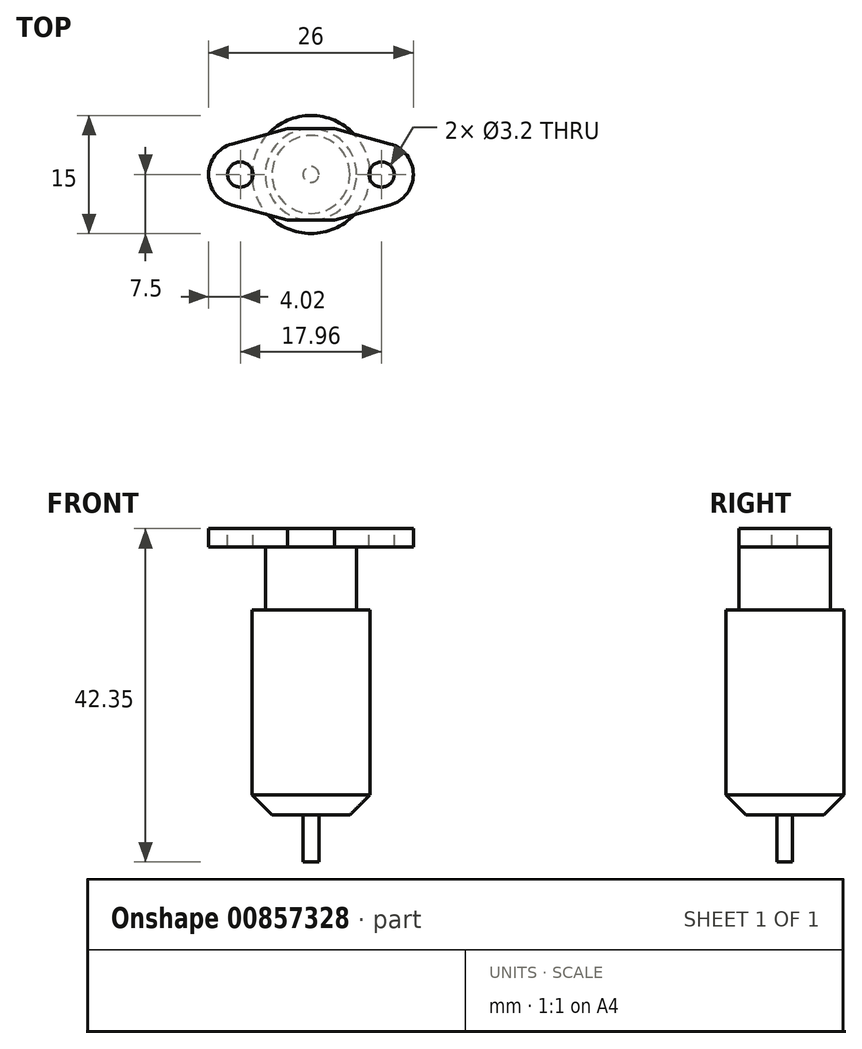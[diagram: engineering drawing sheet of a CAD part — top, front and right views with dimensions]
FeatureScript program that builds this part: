
annotation { "Feature Type Name" : "Feature", "Feature Type Description" : "" }
export const myFeature = defineFeature(function(context is Context, id is Id, definition is map)
    precondition{}
    {
        {
            var Q0;
            Q0=qCreatedBy(makeId("Top.planeOp"),FACE);
            var sketch = newSketch(context, id + "F0", { "sketchPlane" : qUnion([Q0])});
            skCircle(sketch, "E0", {"center": v(-8.98, 0) * mm, "radius": 1.6 * mm});
            skCircle(sketch, "E1", {"center": v(8.98, 0) * mm, "radius": 1.6 * mm});
            skArc(sketch, "E2", {"start": v(10.05, -3.88) * mm, "mid": v(13, 0) * mm, "end": v(10.05, 3.88) * mm});
            skArc(sketch, "E3", {"start": v(-10.05, 3.88) * mm, "mid": v(-13, 0) * mm, "end": v(-10.05, -3.88) * mm});
            skLineSegment(sketch, "E4", {"start": v(-3, 5.82) * mm, "end": v(3, 5.82) * mm});
            skLineSegment(sketch, "E5", {"start": v(-3, -5.82) * mm, "end": v(3, -5.82) * mm});
            skLineSegment(sketch, "E6", {"start": v(-3, 5.82) * mm, "end": v(-10.05, 3.88) * mm});
            skLineSegment(sketch, "E7", {"start": v(3, 5.82) * mm, "end": v(10.05, 3.88) * mm});
            skLineSegment(sketch, "E8", {"start": v(10.05, -3.88) * mm, "end": v(3, -5.82) * mm});
            skLineSegment(sketch, "E9", {"start": v(-3, -5.82) * mm, "end": v(-10.05, -3.88) * mm});
            skSolve(sketch);
        }
        {
            var Q0;
            Q0=makeQuery(id+"F0.imprint","IMPRINT",FACE,{"disambiguationData":[TD([[makeQuery(id+"F0.imprint","IMPRINT",EDGE,{"derivedFrom":sQuery(id+"F0.wireOp",EDGE,"E0")}),-1.0]])]});
            extrude(context, id + "F1", {"entities" : qUnion([Q0]), "oppositeDirection" : true, "depth" : 2.3 * mm, "offsetDistance" : 25 * mm});
        }
        {
            var Q0;
            Q0=qCreatedBy(makeId("Front.planeOp"),FACE);
            var sketch = newSketch(context, id + "F2", { "sketchPlane" : qUnion([Q0])});
            skPoint(sketch, "E10.0", {"position": v(0, -2.3) * mm});
            skLineSegment(sketch, "E11", {"start": v(0, -2.3) * mm, "end": v(5.8, -2.3) * mm});
            skLineSegment(sketch, "E12", {"start": v(5.8, -2.3) * mm, "end": v(5.8, -10.3) * mm});
            skLineSegment(sketch, "E13", {"start": v(5.8, -10.3) * mm, "end": v(7.5, -10.3) * mm});
            skLineSegment(sketch, "E14", {"start": v(7.5, -10.3) * mm, "end": v(7.5, -33.8) * mm});
            skLineSegment(sketch, "E15", {"start": v(7.5, -33.8) * mm, "end": v(4.95, -36.35) * mm});
            skLineSegment(sketch, "E16", {"start": v(4.95, -36.35) * mm, "end": v(1, -36.35) * mm});
            skLineSegment(sketch, "E17", {"start": v(1, -36.35) * mm, "end": v(1, -42.35) * mm});
            skLineSegment(sketch, "E18", {"start": v(1, -42.35) * mm, "end": v(0, -42.35) * mm});
            skLineSegment(sketch, "E19", {"start": v(0, -2.3) * mm, "end": v(0, -42.35) * mm});
            skSolve(sketch);
        }
        {
            var Q0;
            Q0=makeQuery(id+"F2.imprint","IMPRINT",FACE,{"disambiguationData":[TD([[makeQuery(id+"F2.imprint","IMPRINT",EDGE,{"derivedFrom":sQuery(id+"F2.wireOp",EDGE,"E11")}),-1.0]])]});
            var Q1;
            Q1=sQuery(id+"F2.wireOp",EDGE,"E19");
            revolve(context, id + "F3", {"operationType" : NewBodyOperationType.ADD, "surfaceOperationType" : NewSurfaceOperationType.NEW, "entities" : qUnion([Q0]), "axis" : qUnion([Q1]), "revolveType" : RevolveType.FULL});
        }
    });
